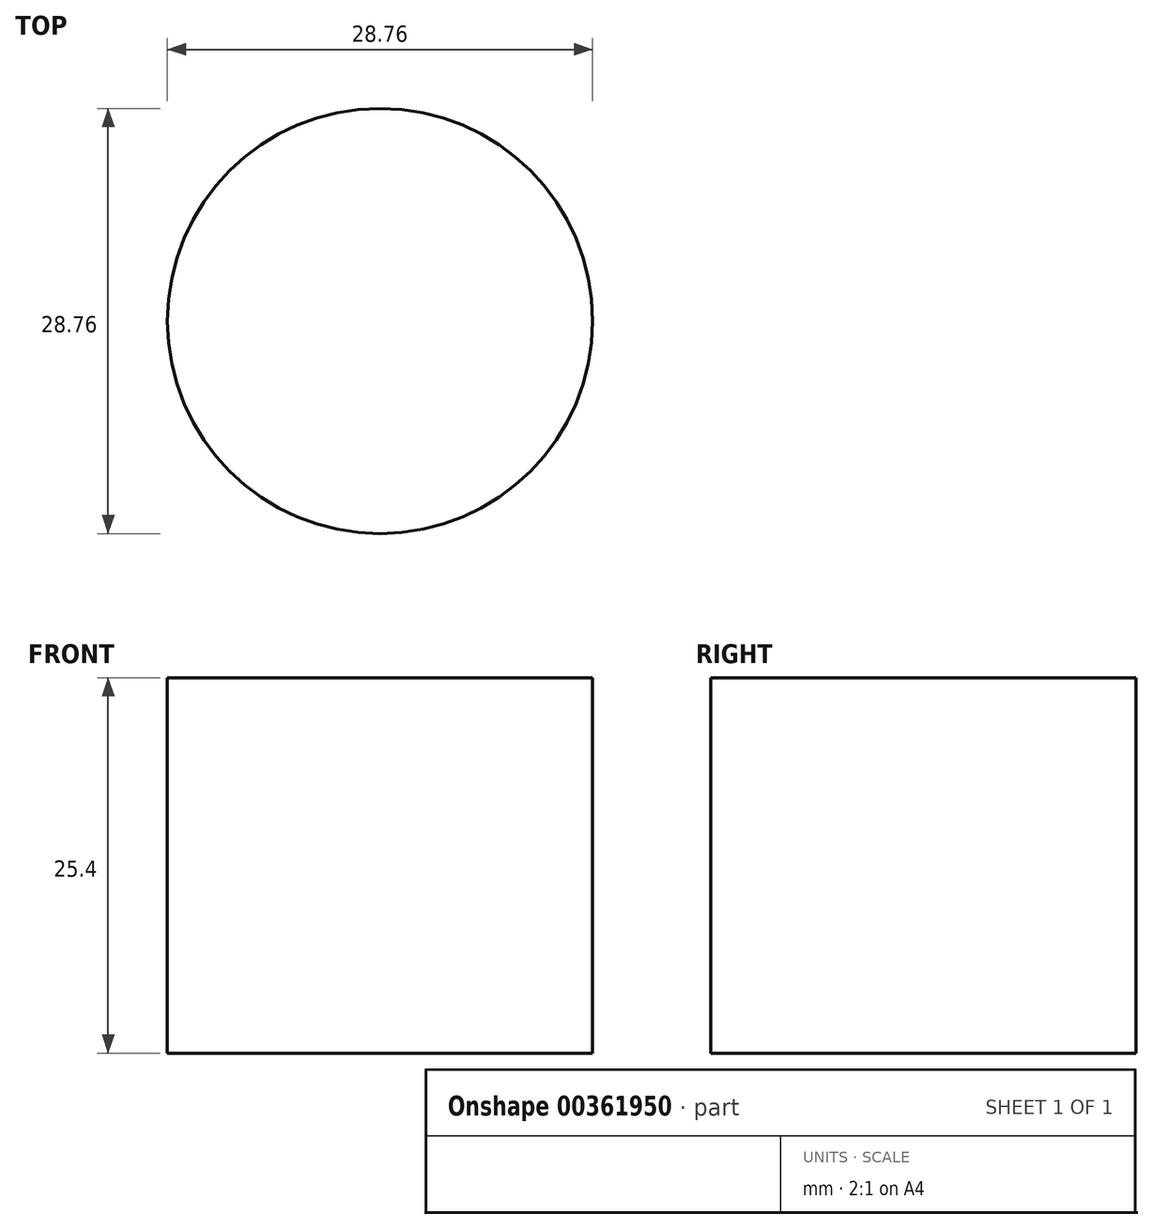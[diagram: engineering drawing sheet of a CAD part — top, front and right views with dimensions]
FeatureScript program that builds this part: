
annotation { "Feature Type Name" : "Feature", "Feature Type Description" : "" }
export const myFeature = defineFeature(function(context is Context, id is Id, definition is map)
    precondition{}
    {
        {
            var Q0;
            Q0=qCreatedBy(makeId("Top.planeOp"),FACE);
            var sketch = newSketch(context, id + "F0", { "sketchPlane" : qUnion([Q0])});
            skCircle(sketch, "E0", {"center": v(0, 0) * mm, "radius": 14.38 * mm});
            skSolve(sketch);
        }
        {
            var Q0;
            Q0 = qSketchRegion(id + "F0", true);
            extrude(context, id + "F1", {"entities" : qUnion([Q0]), "depth" : 25.4 * mm});
        }
    });
